# Revit family: AM0006781_Alacena Savona
name_source: partatom
category: Plumbing Fixtures
units: mm (PartAtom-declared; Revit-internal decimal feet)

## family parameters
Always vertical = Yes
Cut with Voids When Loaded = No
Host = Wall
OmniClass Number = 23.40.40.00
OmniClass Title = Food Service Equipment and Furnishings
Part Type = Normal
Room Calculation Point = No
Round Connector Dimension = Use Diameter
Shared = No

## types (1)
- Type 1
    Alto = 2091 mm  [stored 6.86024 ft]
    Ancho = 592 mm  [stored 1.94226 ft]
    Carga máxima = 65 kg
    Densidad = 15 mm 670 kg./m^3
    Manufacturer = Corona
    Material 1 = Corona_Madera_Taupe
    Material 2 = Corona_Madera_Coñac
    Model = AM0006781
    Peso Neto aproximado = 60,4 kg
    Profundidad = 592 mm  [stored 1.94226 ft]
    Resistencia a la humedad = Hinchamiento < o =8%
    URL = https://corona.co

note: [stored X ft] marks values corroborated as IEEE doubles in the binary element streams (Revit-internal decimal feet)

## geometry (parser evidence)
native form markers: Sweep x8
no freeform markers — native parametric forms only
